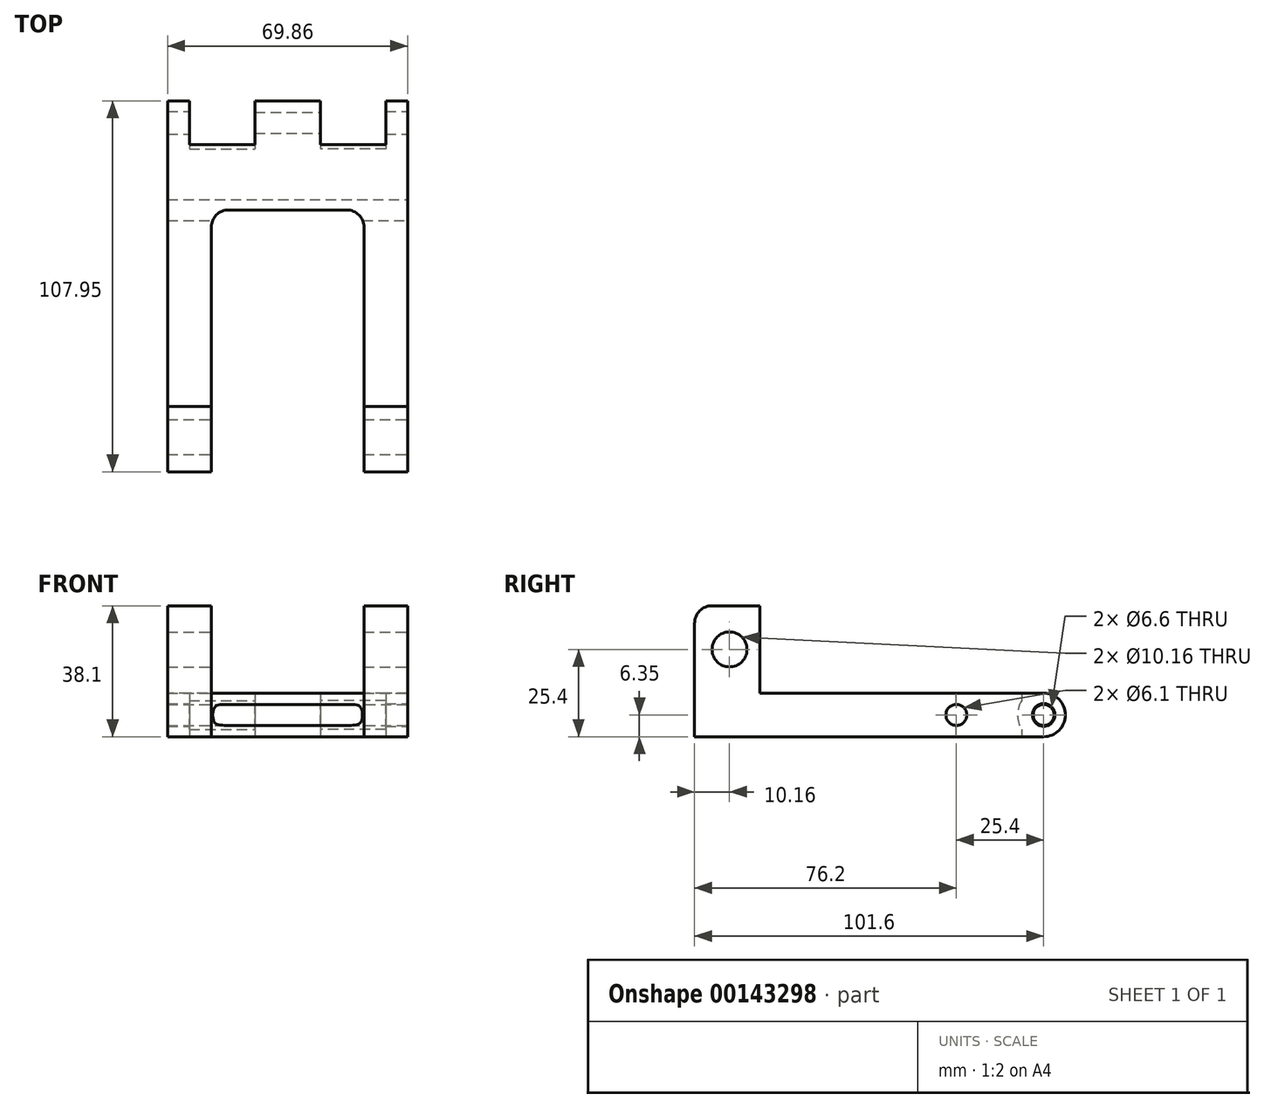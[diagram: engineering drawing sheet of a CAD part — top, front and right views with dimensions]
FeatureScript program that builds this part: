
annotation { "Feature Type Name" : "Feature", "Feature Type Description" : "" }
export const myFeature = defineFeature(function(context is Context, id is Id, definition is map)
    precondition{}
    {
        {
            var Q0;
            Q0=qCreatedBy(makeId("Front.planeOp"),FACE);
            var sketch = newSketch(context, id + "F0", { "sketchPlane" : qUnion([Q0])});
            skLineSegment(sketch, "E0.bottom", {"start": v(34.93, 6.35) * mm, "end": v(-34.93, 6.35) * mm});
            skLineSegment(sketch, "E0.top", {"start": v(34.93, -6.35) * mm, "end": v(-34.93, -6.35) * mm});
            skLineSegment(sketch, "E0.left", {"start": v(34.93, 6.35) * mm, "end": v(34.93, -6.35) * mm});
            skLineSegment(sketch, "E0.right", {"start": v(-34.93, 6.35) * mm, "end": v(-34.93, -6.35) * mm});
            skPoint(sketch, "E0.middle", {"position": v(0, 0) * mm});
            skLineSegment(sketch, "E1.left", {"start": v(28.58, 0) * mm, "end": v(28.58, 0) * mm});
            skLineSegment(sketch, "E1.right", {"start": v(-28.58, 0) * mm, "end": v(-28.58, 0) * mm});
            skLineSegment(sketch, "E2.bottom", {"start": v(34.93, 6.35) * mm, "end": v(22.22, 6.35) * mm});
            skLineSegment(sketch, "E2.top", {"start": v(34.92, 31.75) * mm, "end": v(22.22, 31.75) * mm});
            skLineSegment(sketch, "E2.left", {"start": v(34.93, 6.35) * mm, "end": v(34.93, 31.75) * mm});
            skLineSegment(sketch, "E2.right", {"start": v(22.22, 6.35) * mm, "end": v(22.22, 31.75) * mm});
            skLineSegment(sketch, "E3.bottom", {"start": v(-34.93, 6.35) * mm, "end": v(-22.23, 6.35) * mm});
            skLineSegment(sketch, "E3.top", {"start": v(-34.93, 31.75) * mm, "end": v(-22.23, 31.75) * mm});
            skLineSegment(sketch, "E3.left", {"start": v(-34.93, 6.35) * mm, "end": v(-34.93, 31.75) * mm});
            skLineSegment(sketch, "E3.right", {"start": v(-22.23, 6.35) * mm, "end": v(-22.23, 31.75) * mm});
            skSolve(sketch);
        }
        {
            var Q0;
            Q0 = qSketchRegion(id + "F0", true);
            extrude(context, id + "F1", {"entities" : qUnion([Q0]), "depth" : 101.6 * mm});
        }
        {
            var Q0;
            Q0=makeQuery(id+"F1.opExtrude","SWEPT_FACE",FACE,{"disambiguationData":[OSD([sQuery(id+"F0.wireOp",EDGE,"E0.left"),sQuery(id+"F0.wireOp",EDGE,"E2.left")])]});
            var sketch = newSketch(context, id + "F2", { "sketchPlane" : qUnion([Q0])});
            skLineSegment(sketch, "E4.bottom", {"start": v(0, 31.75) * mm, "end": v(-82.55, 31.75) * mm});
            skLineSegment(sketch, "E4.top", {"start": v(0, 6.35) * mm, "end": v(-82.55, 6.35) * mm});
            skLineSegment(sketch, "E4.left", {"start": v(0, 31.75) * mm, "end": v(0, 6.35) * mm});
            skLineSegment(sketch, "E4.right", {"start": v(-82.55, 31.75) * mm, "end": v(-82.55, 6.35) * mm});
            skLineSegment(sketch, "E5.bottom", {"start": v(-101.6, 31.75) * mm, "end": v(-91.44, 31.75) * mm});
            skLineSegment(sketch, "E5.top", {"start": v(-101.6, 19.05) * mm, "end": v(-91.44, 19.05) * mm});
            skLineSegment(sketch, "E5.left", {"start": v(-101.6, 31.75) * mm, "end": v(-101.6, 19.05) * mm});
            skLineSegment(sketch, "E5.right", {"start": v(-91.44, 31.75) * mm, "end": v(-91.44, 19.05) * mm});
            skCircle(sketch, "E6", {"center": v(-91.44, 19.05) * mm, "radius": 5.08 * mm});
            skSolve(sketch);
        }
        {
            var Q0;
            {var subQ5=sQuery(id+"F2.wireOp",EDGE,"AO0ncT39-5shy-5VOk-pr8N-apeMBWnhLY2L.bottom");Q0=makeQuery(id+"F2.imprint","IMPRINT",FACE,{"disambiguationData":[TD([[makeQuery(id+"F2.imprint","IMPRINT",EDGE,{"derivedFrom":subQ5}),-1.0]])]});}
            var Q1;
            {var subQ5=sQuery(id+"F2.wireOp",EDGE,"AO0ncT39-5shy-5VOk-pr8N-apeMBWnhLY2L.top");Q1=makeQuery(id+"F2.imprint","IMPRINT",FACE,{"disambiguationData":[TD([[makeQuery(id+"F2.imprint","IMPRINT",EDGE,{"derivedFrom":subQ5}),1.0]])]});}
            var Q2;
            Q2=makeQuery(id+"F2.imprint","IMPRINT",FACE,{"disambiguationData":[TD([[makeQuery(id+"F2.imprint","IMPRINT",EDGE,{"derivedFrom":sQuery(id+"F2.wireOp",EDGE,"E4.bottom")}),-1.0]])]});
            var Q3;
            {var subQ0=sQuery(id+"F2.wireOp",EDGE,"E5.right");var subQ1=sQuery(id+"F2.wireOp",EDGE,"E5.top");var subQ2=makeQuery(id+"F2.imprint","INTERSECT",VERTEX,{"derivedFrom":[subQ1,subQ0]});Q3=makeQuery(id+"F2.imprint","IMPRINT",FACE,{"disambiguationData":[TD([[makeQuery(id+"F2.imprint","IMPRINT",EDGE,{"disambiguationData":[TD([[subQ2,1.0]])],"derivedFrom":subQ1}),-1.0]])]});}
            var Q4;
            {var subQ0=sQuery(id+"F2.wireOp",EDGE,"E5.right");var subQ1=sQuery(id+"F2.wireOp",EDGE,"E5.top");var subQ2=makeQuery(id+"F2.imprint","INTERSECT",VERTEX,{"derivedFrom":[subQ1,subQ0]});Q4=makeQuery(id+"F2.imprint","IMPRINT",FACE,{"disambiguationData":[TD([[makeQuery(id+"F2.imprint","IMPRINT",EDGE,{"disambiguationData":[TD([[subQ2,1.0]])],"derivedFrom":subQ1}),1.0]])]});}
            extrude(context, id + "F3", {"entities" : qUnion([Q0, Q1, Q2, Q3, Q4]), "operationType" : NewBodyOperationType.REMOVE, "endBound" : BoundingType.THROUGH_ALL, "oppositeDirection" : true, "depth" : 25.4 * mm});
        }
        {
            var Q0;
            Q0=makeQuery(id+"F3.boolean.opBoolean","MERGE",FACE,{"derivedFrom":[makeQuery(id+"F1.opExtrude","SWEPT_FACE",FACE,{"disambiguationData":[OSD([sQuery(id+"F0.wireOp",EDGE,"E0.bottom")])]}),makeQuery(id+"F3.opExtrude","SWEPT_FACE",FACE,{"disambiguationData":[OSD([sQuery(id+"F2.wireOp",EDGE,"E4.top")])]})]});
            var sketch = newSketch(context, id + "F4", { "sketchPlane" : qUnion([Q0])});
            skLineSegment(sketch, "E7.bottom", {"start": v(-22.23, -76.2) * mm, "end": v(22.22, -76.2) * mm});
            skLineSegment(sketch, "E7.top", {"start": v(-22.23, -25.4) * mm, "end": v(22.22, -25.4) * mm});
            skLineSegment(sketch, "E7.left", {"start": v(-22.23, -76.2) * mm, "end": v(-22.23, -25.4) * mm});
            skLineSegment(sketch, "E7.right", {"start": v(22.22, -76.2) * mm, "end": v(22.22, -25.4) * mm});
            skLineSegment(sketch, "E8.top", {"start": v(-22.23, -101.6) * mm, "end": v(22.22, -101.6) * mm});
            skLineSegment(sketch, "E8.left", {"start": v(-22.23, -76.2) * mm, "end": v(-22.23, -101.6) * mm});
            skLineSegment(sketch, "E8.right", {"start": v(22.22, -76.2) * mm, "end": v(22.22, -101.6) * mm});
            skSolve(sketch);
        }
        {
            var Q0;
            Q0 = qSketchRegion(id + "F4", true);
            extrude(context, id + "F5", {"entities" : qUnion([Q0]), "operationType" : NewBodyOperationType.REMOVE, "oppositeDirection" : true, "depth" : 25.4 * mm});
        }
        {
            var Q0;
            Q0=makeQuery(id+"F1.opExtrude","CAP_EDGE",EDGE,{"disambiguationData":[OSD([sQuery(id+"F0.wireOp",EDGE,"E3.top")])],"isStart":false});
            var Q1;
            {var subQ0=sQuery(id+"F2.wireOp",EDGE,"E4.right");Q1=makeQuery(id+"F3.boolean.opBoolean","COPY",EDGE,{"disambiguationData":[TD([makeQuery(id+"F1.opExtrude","SWEPT_FACE",FACE,{"disambiguationData":[OSD([sQuery(id+"F0.wireOp",EDGE,"E3.top")])]})])],"derivedFrom":makeQuery(id+"F3.opExtrude","SWEPT_EDGE",EDGE,{"disambiguationData":[OSD([sQuery(id+"F0.wireOp",EDGE,"E2.top"),sQuery(id+"F0.wireOp",EDGE,"E2.left"),sQuery(id+"F2.wireOp",EDGE,"E4.bottom"),subQ0])]})});}
            var Q2;
            Q2=makeQuery(id+"F1.opExtrude","CAP_EDGE",EDGE,{"disambiguationData":[OSD([sQuery(id+"F0.wireOp",EDGE,"E2.top")])],"isStart":false});
            var Q3;
            {var subQ0=sQuery(id+"F0.wireOp",EDGE,"E2.left");var subQ1=sQuery(id+"F2.wireOp",EDGE,"E4.right");var subQ2=sQuery(id+"F0.wireOp",EDGE,"E2.top");Q3=makeQuery(id+"F3.boolean.opBoolean","COPY",EDGE,{"disambiguationData":[TD([makeQuery(id+"F1.opExtrude","SWEPT_FACE",FACE,{"disambiguationData":[OSD([subQ2])]})])],"derivedFrom":makeQuery(id+"F3.opExtrude","SWEPT_EDGE",EDGE,{"disambiguationData":[OSD([subQ2,subQ0,sQuery(id+"F2.wireOp",EDGE,"E4.bottom"),subQ1])]})});}
            var Q4;
            {var subQ0=sQuery(id+"F2.wireOp",EDGE,"AO0ncT39-5shy-5VOk-pr8N-apeMBWnhLY2L.right");Q4=makeQuery(id+"F3.boolean.opBoolean","COPY",EDGE,{"disambiguationData":[topologyDisambiguationEdgeConnected([makeQuery(id+"F1.opExtrude","SWEPT_FACE",FACE,{"disambiguationData":[OSD([sQuery(id+"F0.wireOp",EDGE,"E3.top")])]})])],"derivedFrom":makeQuery(id+"F3.opExtrude","SWEPT_EDGE",EDGE,{"disambiguationData":[OSD([sQuery(id+"F2.wireOp",EDGE,"E5.bottom"),sQuery(id+"F2.wireOp",EDGE,"AO0ncT39-5shy-5VOk-pr8N-apeMBWnhLY2L.bottom"),subQ0])]})});}
            var Q5;
            {var subQ0=sQuery(id+"F2.wireOp",EDGE,"AO0ncT39-5shy-5VOk-pr8N-apeMBWnhLY2L.right");Q5=makeQuery(id+"F3.boolean.opBoolean","COPY",EDGE,{"disambiguationData":[topologyDisambiguationEdgeConnected([makeQuery(id+"F1.opExtrude","SWEPT_FACE",FACE,{"disambiguationData":[OSD([sQuery(id+"F0.wireOp",EDGE,"E2.top")])]})])],"derivedFrom":makeQuery(id+"F3.opExtrude","SWEPT_EDGE",EDGE,{"disambiguationData":[OSD([sQuery(id+"F2.wireOp",EDGE,"E5.bottom"),sQuery(id+"F2.wireOp",EDGE,"AO0ncT39-5shy-5VOk-pr8N-apeMBWnhLY2L.bottom"),subQ0])]})});}
            fillet(context, id + "F6", {"entities" : qUnion([Q0, Q1, Q2, Q3, Q4, Q5]), "radius" : 5.08 * mm, "tangentPropagation" : true, "allowEdgeOverflow" : false});
        }
        {
            var Q0;
            Q0=makeQuery(id+"F1.opExtrude","SWEPT_FACE",FACE,{"disambiguationData":[OSD([sQuery(id+"F0.wireOp",EDGE,"E0.left"),sQuery(id+"F0.wireOp",EDGE,"E2.left")])]});
            var sketch = newSketch(context, id + "F7", { "sketchPlane" : qUnion([Q0])});
            skCircle(sketch, "E9", {"center": v(0, 0) * mm, "radius": 6.35 * mm});
            skCircle(sketch, "E10", {"center": v(0, 0) * mm, "radius": 3.3 * mm});
            skSolve(sketch);
        }
        {
            var Q0;
            Q0 = qSketchRegion(id + "F7", true);
            var Q1;
            Q1=makeQuery(id+"F1.opExtrude","SWEPT_FACE",FACE,{"disambiguationData":[OSD([sQuery(id+"F0.wireOp",EDGE,"E0.right"),sQuery(id+"F0.wireOp",EDGE,"E3.left")])]});
            extrude(context, id + "F8", {"entities" : qUnion([Q0]), "operationType" : NewBodyOperationType.ADD, "endBound" : BoundingType.UP_TO_SURFACE, "oppositeDirection" : true, "endBoundEntityFace" : qUnion([Q1]), "depth" : 25.4 * mm});
        }
        {
            var Q0;
            Q0=makeQuery(id+"F8.boolean.opBoolean","MERGE",FACE,{"derivedFrom":[makeQuery(id+"F1.opExtrude","SWEPT_FACE",FACE,{"disambiguationData":[OSD([sQuery(id+"F0.wireOp",EDGE,"E0.left"),sQuery(id+"F0.wireOp",EDGE,"E2.left")])]}),makeQuery(id+"F8.opExtrude","CAP_FACE",FACE,{"disambiguationData":[OSD([sQuery(id+"F7.wireOp",EDGE,"E9"),sQuery(id+"F7.wireOp",EDGE,"E10")])],"isStart":true})]});
            var sketch = newSketch(context, id + "F9", { "sketchPlane" : qUnion([Q0])});
            skCircle(sketch, "E11", {"center": v(0, 0) * mm, "radius": 3.3 * mm});
            skSolve(sketch);
        }
        {
            var Q0;
            Q0 = qSketchRegion(id + "F9", true);
            extrude(context, id + "F10", {"entities" : qUnion([Q0]), "operationType" : NewBodyOperationType.REMOVE, "endBound" : BoundingType.THROUGH_ALL, "oppositeDirection" : true, "depth" : 25.4 * mm});
        }
        {
            var Q0;
            Q0=qCreatedBy(makeId("Front.planeOp"),FACE);
            var sketch = newSketch(context, id + "F11", { "sketchPlane" : qUnion([Q0])});
            skLineSegment(sketch, "E12", {"start": v(0, 0) * mm, "end": v(-19.05, 0) * mm});
            skLineSegment(sketch, "E13", {"start": v(-19.05, 0) * mm, "end": v(0, 0) * mm});
            skLineSegment(sketch, "E14", {"start": v(0, 0) * mm, "end": v(19.05, 0) * mm});
            skLineSegment(sketch, "E15", {"start": v(19.05, 0) * mm, "end": v(0, 0) * mm});
            skLineSegment(sketch, "E16.bottom", {"start": v(9.53, 10.15) * mm, "end": v(28.58, 10.15) * mm});
            skLineSegment(sketch, "E16.top", {"start": v(9.52, -10.15) * mm, "end": v(28.57, -10.15) * mm});
            skLineSegment(sketch, "E16.left", {"start": v(9.53, 10.15) * mm, "end": v(9.52, -10.15) * mm});
            skLineSegment(sketch, "E16.right", {"start": v(28.58, 10.15) * mm, "end": v(28.57, -10.15) * mm});
            skPoint(sketch, "E16.middle", {"position": v(19.05, 0) * mm});
            skLineSegment(sketch, "E17.bottom", {"start": v(-28.58, 12.2) * mm, "end": v(-9.53, 12.2) * mm});
            skLineSegment(sketch, "E17.top", {"start": v(-28.58, -12.2) * mm, "end": v(-9.53, -12.2) * mm});
            skLineSegment(sketch, "E17.left", {"start": v(-28.58, 12.2) * mm, "end": v(-28.58, -12.2) * mm});
            skLineSegment(sketch, "E17.right", {"start": v(-9.53, 12.2) * mm, "end": v(-9.53, -12.2) * mm});
            skPoint(sketch, "E17.middle", {"position": v(-19.05, 0) * mm});
            skSolve(sketch);
        }
        {
            var Q0;
            Q0 = qSketchRegion(id + "F11", true);
            extrude(context, id + "F12", {"entities" : qUnion([Q0]), "operationType" : NewBodyOperationType.REMOVE, "oppositeDirection" : true, "depth" : 12.7 * mm, "symmetric" : true});
        }
        {
            var Q0;
            Q0=makeQuery(id+"F12.boolean.opBoolean","COPY",FACE,{"derivedFrom":makeQuery(id+"F12.opExtrude","SWEPT_FACE",FACE,{"disambiguationData":[OSD([sQuery(id+"F11.wireOp",EDGE,"E16.left")])]})});
            var sketch = newSketch(context, id + "F13", { "sketchPlane" : qUnion([Q0])});
            skCircle(sketch, "E18", {"center": v(0, 0) * mm, "radius": 3.05 * mm});
            skCircle(sketch, "E19", {"center": v(0, 0) * mm, "radius": 4.85 * mm});
            skSolve(sketch);
        }
        {
            var Q0;
            Q0 = qSketchRegion(id + "F13", true);
            var Q1;
            Q1=makeQuery(id+"F12.boolean.opBoolean","COPY",FACE,{"derivedFrom":makeQuery(id+"F12.opExtrude","SWEPT_FACE",FACE,{"disambiguationData":[OSD([sQuery(id+"F11.wireOp",EDGE,"E17.right")])]})});
            extrude(context, id + "F14", {"entities" : qUnion([Q0]), "operationType" : NewBodyOperationType.ADD, "endBound" : BoundingType.UP_TO_SURFACE, "oppositeDirection" : true, "endBoundEntityFace" : qUnion([Q1]), "depth" : 25.4 * mm});
        }
        {
            var Q0;
            Q0=makeQuery(id+"F8.boolean.opBoolean","MERGE",FACE,{"derivedFrom":[makeQuery(id+"F1.opExtrude","SWEPT_FACE",FACE,{"disambiguationData":[OSD([sQuery(id+"F0.wireOp",EDGE,"E0.left"),sQuery(id+"F0.wireOp",EDGE,"E2.left")])]}),makeQuery(id+"F8.opExtrude","CAP_FACE",FACE,{"disambiguationData":[OSD([sQuery(id+"F7.wireOp",EDGE,"E9"),sQuery(id+"F7.wireOp",EDGE,"E10")])],"isStart":true})]});
            var sketch = newSketch(context, id + "F15", { "sketchPlane" : qUnion([Q0])});
            skLineSegment(sketch, "E20", {"start": v(0, 0) * mm, "end": v(-25.4, 0) * mm});
            skLineSegment(sketch, "E21", {"start": v(-25.4, 0) * mm, "end": v(0, 0) * mm});
            skCircle(sketch, "E22", {"center": v(-25.4, 0) * mm, "radius": 3.05 * mm});
            skSolve(sketch);
        }
        {
            var Q0;
            Q0 = qSketchRegion(id + "F15", true);
            extrude(context, id + "F16", {"entities" : qUnion([Q0]), "operationType" : NewBodyOperationType.REMOVE, "endBound" : BoundingType.THROUGH_ALL, "oppositeDirection" : true, "depth" : 25.4 * mm});
        }
        {
            var Q0;
            Q0=makeQuery(id+"F5.boolean.opBoolean","COPY",EDGE,{"derivedFrom":makeQuery(id+"F5.opExtrude","SWEPT_EDGE",EDGE,{"disambiguationData":[OSD([sQuery(id+"F4.wireOp",EDGE,"E7.top"),sQuery(id+"F4.wireOp",EDGE,"E7.left")])]})});
            var Q1;
            Q1=makeQuery(id+"F5.boolean.opBoolean","COPY",EDGE,{"derivedFrom":makeQuery(id+"F5.opExtrude","SWEPT_EDGE",EDGE,{"disambiguationData":[OSD([sQuery(id+"F4.wireOp",EDGE,"E7.top"),sQuery(id+"F4.wireOp",EDGE,"E7.right")])]})});
            fillet(context, id + "F17", {"entities" : qUnion([Q0, Q1]), "radius" : 5.08 * mm, "tangentPropagation" : true, "allowEdgeOverflow" : false});
        }
        {
            var Q0;
            Q0=makeQuery(id+"F14.boolean.opBoolean","MERGE",FACE,{"derivedFrom":[makeQuery(id+"F12.boolean.opBoolean","COPY",FACE,{"derivedFrom":makeQuery(id+"F12.opExtrude","SWEPT_FACE",FACE,{"disambiguationData":[OSD([sQuery(id+"F11.wireOp",EDGE,"E16.left")])]})}),makeQuery(id+"F14.opExtrude","CAP_FACE",FACE,{"disambiguationData":[OSD([sQuery(id+"F13.wireOp",EDGE,"E18"),sQuery(id+"F13.wireOp",EDGE,"E19")])],"isStart":true})]});
            var sketch = newSketch(context, id + "F18", { "sketchPlane" : qUnion([Q0])});
            skCircle(sketch, "E23", {"center": v(0, 0) * mm, "radius": 7.62 * mm});
            skSolve(sketch);
        }
        {
            var Q0;
            Q0 = qSketchRegion(id + "F18", true);
            var Q1;
            Q1=makeQuery(id+"F12.boolean.opBoolean","COPY",FACE,{"derivedFrom":makeQuery(id+"F12.opExtrude","SWEPT_FACE",FACE,{"disambiguationData":[OSD([sQuery(id+"F11.wireOp",EDGE,"E16.right")])]})});
            extrude(context, id + "F19", {"entities" : qUnion([Q0]), "operationType" : NewBodyOperationType.REMOVE, "endBound" : BoundingType.UP_TO_SURFACE, "endBoundEntityFace" : qUnion([Q1]), "depth" : 25.4 * mm});
        }
        {
            var Q0;
            {var subQ0=sQuery(id+"F11.wireOp",EDGE,"E17.right");Q0=makeQuery(id+"F14.boolean.opBoolean","MERGE",FACE,{"derivedFrom":[makeQuery(id+"F12.boolean.opBoolean","COPY",FACE,{"derivedFrom":makeQuery(id+"F12.opExtrude","SWEPT_FACE",FACE,{"disambiguationData":[OSD([subQ0])]})}),makeQuery(id+"F14.opExtrude","CAP_FACE",FACE,{"disambiguationData":[OSD([subQ0])],"isStart":false})]});}
            var sketch = newSketch(context, id + "F20", { "sketchPlane" : qUnion([Q0])});
            skCircle(sketch, "E24", {"center": v(0, 0) * mm, "radius": 7.62 * mm});
            skSolve(sketch);
        }
        {
            var Q0;
            Q0 = qSketchRegion(id + "F20", true);
            var Q1;
            Q1=makeQuery(id+"F12.boolean.opBoolean","COPY",FACE,{"derivedFrom":makeQuery(id+"F12.opExtrude","SWEPT_FACE",FACE,{"disambiguationData":[OSD([sQuery(id+"F11.wireOp",EDGE,"E17.left")])]})});
            extrude(context, id + "F21", {"entities" : qUnion([Q0]), "operationType" : NewBodyOperationType.REMOVE, "endBound" : BoundingType.UP_TO_SURFACE, "endBoundEntityFace" : qUnion([Q1]), "depth" : 25.4 * mm});
        }
    });
